# Revit family: 12302_GEK2
name_source: partatom
category: Air Terminals
revit_build: Autodesk Revit MEP 2012 (Build: 20110309_2315(x64)
units: mm (PartAtom-declared; Revit-internal decimal feet)

## types (1)
- GEK2
    Conect_Horizontal = 23 3/4"
    Conect_Vertical = 23 3/4"
    Cuello Cuadrado Min-Max = 6"x6" a 36"x36"
    Cuello Rectangular Min-Max = 8"x6" a 48"x36"
    Description = Rejilla de Transferencia
    Función = Transferencia
    Inclinación = 30 grados
    Incrementos de Cuello = de 2"
    Manufacturer = INNES
    Material = Aluminio
    Medida_Requerida_Horizontal = 24"
    Medida_Requerida_Vertical = 24"
    Model = GEK2
    Nota1 = .
    Posición de Instalación = Muro
    Tipo de Cuello = Cuadrado/Rectangular
    Type Comments = Aletas fijas tipo "K"
    URL = https://www.innes.com.mx
    Var1 = 24
    Var2 = 24
    Var3 = 24"
    Var4 = 24"
    Visible_Texto = No

## geometry (parser evidence)
native form markers: Sweep x8
no freeform markers — native parametric forms only
